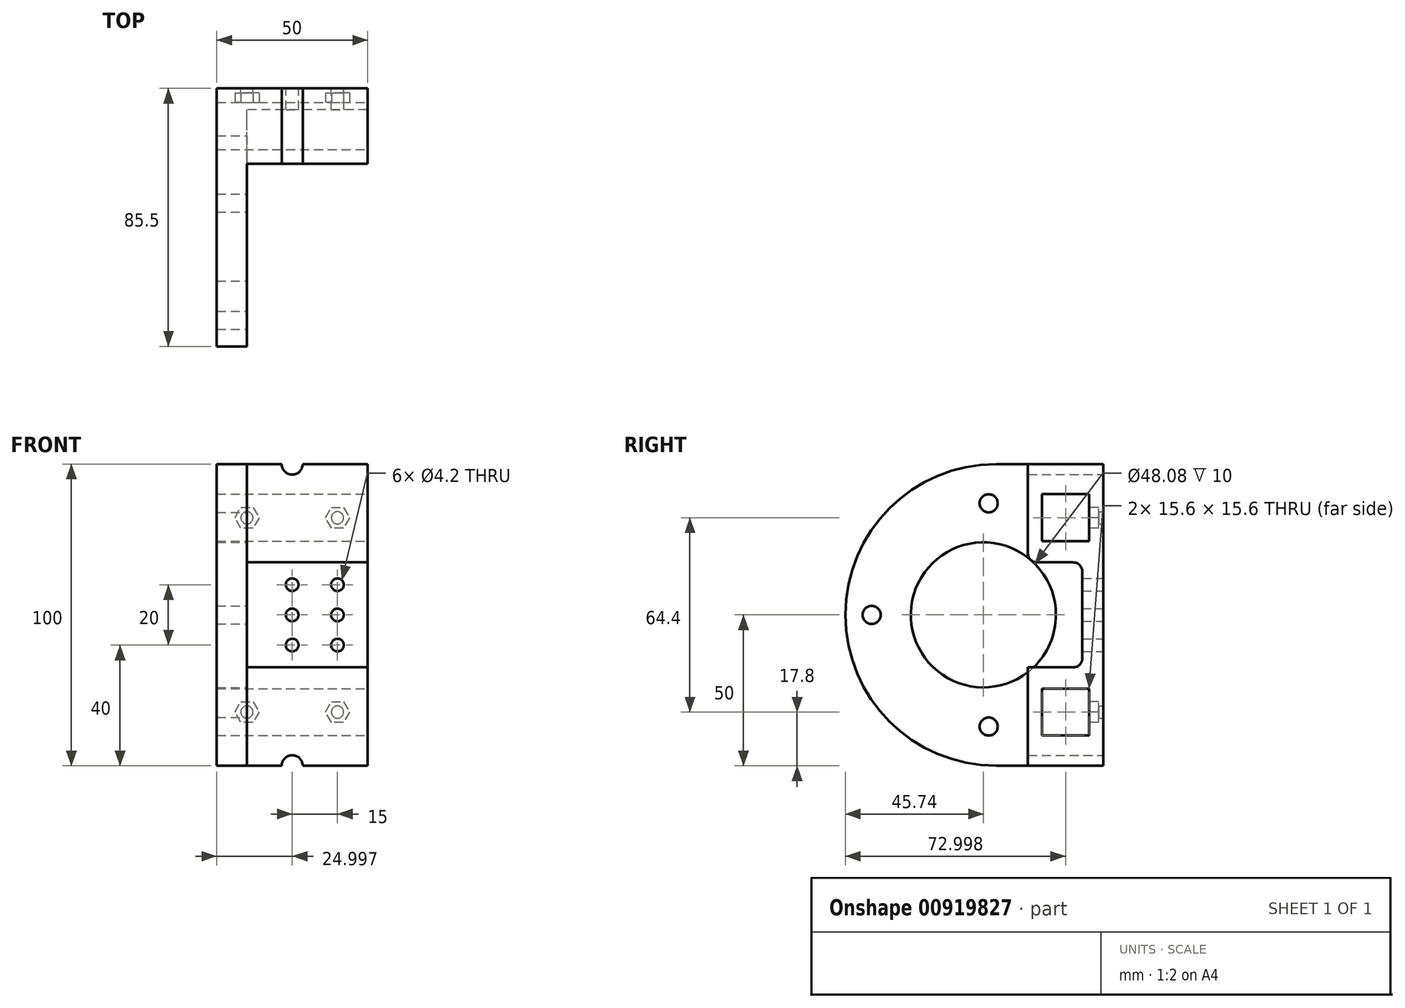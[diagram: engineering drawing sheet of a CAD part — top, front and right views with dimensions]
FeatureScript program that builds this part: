
annotation { "Feature Type Name" : "Feature", "Feature Type Description" : "" }
export const myFeature = defineFeature(function(context is Context, id is Id, definition is map)
    precondition{}
    {
        {
            var Q0;
            Q0=qCreatedBy(makeId("Top.planeOp"),FACE);
            var sketch = newSketch(context, id + "F0", { "sketchPlane" : qUnion([Q0])});
            skLineSegment(sketch, "E0", {"start": v(5.18, 41.2) * mm, "end": v(-44.82, 41.2) * mm});
            skLineSegment(sketch, "E1", {"start": v(-44.82, 41.2) * mm, "end": v(-44.82, -44.3) * mm});
            skLineSegment(sketch, "E2", {"start": v(-44.82, -44.3) * mm, "end": v(-34.82, -44.3) * mm});
            skLineSegment(sketch, "E3", {"start": v(-34.82, -44.3) * mm, "end": v(-34.82, 16.2) * mm});
            skLineSegment(sketch, "E4", {"start": v(-34.82, 16.2) * mm, "end": v(5.18, 16.2) * mm});
            skLineSegment(sketch, "E5", {"start": v(5.18, 16.2) * mm, "end": v(5.18, 41.2) * mm});
            skLineSegment(sketch, "E6.bottom", {"start": v(-27.62, -6.3) * mm, "end": v(-7.62, -6.3) * mm, "construction": true});
            skLineSegment(sketch, "E6.top", {"start": v(-27.62, -26.3) * mm, "end": v(-7.62, -26.3) * mm, "construction": true});
            skLineSegment(sketch, "E6.left", {"start": v(-27.62, -6.3) * mm, "end": v(-27.62, -26.3) * mm, "construction": true});
            skLineSegment(sketch, "E6.right", {"start": v(-7.62, -6.3) * mm, "end": v(-7.62, -26.3) * mm, "construction": true});
            skSolve(sketch);
        }
        {
            var Q0;
            Q0=makeQuery(id+"F0.imprint","IMPRINT",FACE,{"disambiguationData":[TD([[makeQuery(id+"F0.imprint","IMPRINT",EDGE,{"derivedFrom":sQuery(id+"F0.wireOp",EDGE,"E0")}),1.0]])]});
            var Q1;
            Q1 = qSketchRegion(id + "F0", true);
            extrude(context, id + "F1", {"entities" : qUnion([Q0, Q1]), "depth" : 100 * mm, "offsetDistance" : 25 * mm});
        }
        {
            var Q0;
            Q0=makeQuery(id+"F1.opExtrude","SWEPT_FACE",FACE,{"disambiguationData":[OSD([sQuery(id+"F0.wireOp",EDGE,"E5")])]});
            var sketch = newSketch(context, id + "F2", { "sketchPlane" : qUnion([Q0])});
            skLineSegment(sketch, "E7.bottom", {"start": v(36.5, 10) * mm, "end": v(20.9, 10) * mm});
            skLineSegment(sketch, "E7.top", {"start": v(36.5, 25.6) * mm, "end": v(20.9, 25.6) * mm});
            skLineSegment(sketch, "E7.left", {"start": v(36.5, 10) * mm, "end": v(36.5, 25.6) * mm});
            skLineSegment(sketch, "E7.right", {"start": v(20.9, 10) * mm, "end": v(20.9, 25.6) * mm});
            skPoint(sketch, "E7.middle", {"position": v(28.7, 17.8) * mm});
            skPoint(sketch, "E7.middle.positionSnap0", {"position": v(28.7, 0) * mm});
            skPoint(sketch, "E7.centerSnap0", {"position": v(28.7, 0) * mm});
            skLineSegment(sketch, "E8.bottom", {"start": v(36.5, 74.4) * mm, "end": v(20.9, 74.4) * mm});
            skLineSegment(sketch, "E8.top", {"start": v(36.5, 90) * mm, "end": v(20.9, 90) * mm});
            skLineSegment(sketch, "E8.left", {"start": v(36.5, 74.4) * mm, "end": v(36.5, 90) * mm});
            skLineSegment(sketch, "E8.right", {"start": v(20.9, 74.4) * mm, "end": v(20.9, 90) * mm});
            skPoint(sketch, "E8.middle", {"position": v(28.7, 82.2) * mm});
            skPoint(sketch, "E8.middle.positionSnap0", {"position": v(28.7, 100) * mm});
            skPoint(sketch, "E8.centerSnap0", {"position": v(28.7, 100) * mm});
            skSolve(sketch);
        }
        {
            var Q0;
            Q0 = qSketchRegion(id + "F2", true);
            extrude(context, id + "F3", {"entities" : qUnion([Q0]), "operationType" : NewBodyOperationType.REMOVE, "oppositeDirection" : true, "depth" : 134.9 * mm, "offsetDistance" : 25 * mm});
        }
        {
            var Q0;
            Q0=makeQuery(id+"F3.boolean.opBoolean","COPY",FACE,{"derivedFrom":makeQuery(id+"F3.opExtrude","SWEPT_FACE",FACE,{"disambiguationData":[OSD([sQuery(id+"F2.wireOp",EDGE,"E8.left")])]})});
            var sketch = newSketch(context, id + "F4", { "sketchPlane" : qUnion([Q0])});
            skCircle(sketch, "E9.cCircle", {"center": v(-4.82, 82.2) * mm, "radius": 3.46 * mm, "construction": true});
            skLineSegment(sketch, "E9.0", {"start": v(-6.82, 85.66) * mm, "end": v(-2.82, 85.66) * mm});
            skLineSegment(sketch, "E9.1", {"start": v(-2.82, 85.66) * mm, "end": v(-0.83, 82.2) * mm});
            skLineSegment(sketch, "E9.2", {"start": v(-0.83, 82.2) * mm, "end": v(-2.82, 78.74) * mm});
            skLineSegment(sketch, "E9.3", {"start": v(-2.82, 78.74) * mm, "end": v(-6.82, 78.74) * mm});
            skLineSegment(sketch, "E9.4", {"start": v(-6.82, 78.74) * mm, "end": v(-8.82, 82.2) * mm});
            skLineSegment(sketch, "E9.5", {"start": v(-8.82, 82.2) * mm, "end": v(-6.82, 85.66) * mm});
            skPoint(sketch, "E9.0.midPoint", {"position": v(-4.82, 85.66) * mm});
            skCircle(sketch, "E10.cCircle", {"center": v(-34.82, 82.2) * mm, "radius": 3.46 * mm, "construction": true});
            skLineSegment(sketch, "E10.0", {"start": v(-36.82, 85.66) * mm, "end": v(-32.82, 85.66) * mm});
            skLineSegment(sketch, "E10.1", {"start": v(-32.82, 85.66) * mm, "end": v(-30.83, 82.2) * mm});
            skLineSegment(sketch, "E10.2", {"start": v(-30.83, 82.2) * mm, "end": v(-32.82, 78.74) * mm});
            skLineSegment(sketch, "E10.3", {"start": v(-32.82, 78.74) * mm, "end": v(-36.82, 78.74) * mm});
            skLineSegment(sketch, "E10.4", {"start": v(-36.82, 78.74) * mm, "end": v(-38.82, 82.2) * mm});
            skLineSegment(sketch, "E10.5", {"start": v(-38.82, 82.2) * mm, "end": v(-36.82, 85.66) * mm});
            skPoint(sketch, "E10.0.midPoint", {"position": v(-34.82, 85.66) * mm});
            skCircle(sketch, "E11.cCircle", {"center": v(-34.82, 17.8) * mm, "radius": 3.46 * mm, "construction": true});
            skLineSegment(sketch, "E11.0", {"start": v(-36.82, 21.26) * mm, "end": v(-32.82, 21.26) * mm});
            skLineSegment(sketch, "E11.1", {"start": v(-32.82, 21.26) * mm, "end": v(-30.83, 17.8) * mm});
            skLineSegment(sketch, "E11.2", {"start": v(-30.83, 17.8) * mm, "end": v(-32.82, 14.34) * mm});
            skLineSegment(sketch, "E11.3", {"start": v(-32.82, 14.34) * mm, "end": v(-36.82, 14.34) * mm});
            skLineSegment(sketch, "E11.4", {"start": v(-36.82, 14.34) * mm, "end": v(-38.82, 17.8) * mm});
            skLineSegment(sketch, "E11.5", {"start": v(-38.82, 17.8) * mm, "end": v(-36.82, 21.26) * mm});
            skPoint(sketch, "E11.0.midPoint", {"position": v(-34.82, 21.26) * mm});
            skPoint(sketch, "E12", {"position": v(-44.82, 82.2) * mm});
            skCircle(sketch, "E13.cCircle", {"center": v(-4.82, 17.8) * mm, "radius": 3.46 * mm, "construction": true});
            skLineSegment(sketch, "E13.0", {"start": v(-6.82, 21.26) * mm, "end": v(-2.82, 21.26) * mm});
            skLineSegment(sketch, "E13.1", {"start": v(-2.82, 21.26) * mm, "end": v(-0.83, 17.8) * mm});
            skLineSegment(sketch, "E13.2", {"start": v(-0.83, 17.8) * mm, "end": v(-2.82, 14.34) * mm});
            skLineSegment(sketch, "E13.3", {"start": v(-2.82, 14.34) * mm, "end": v(-6.82, 14.34) * mm});
            skLineSegment(sketch, "E13.4", {"start": v(-6.82, 14.34) * mm, "end": v(-8.82, 17.8) * mm});
            skLineSegment(sketch, "E13.5", {"start": v(-8.82, 17.8) * mm, "end": v(-6.82, 21.26) * mm});
            skPoint(sketch, "E13.0.midPoint", {"position": v(-4.82, 21.26) * mm});
            skSolve(sketch);
        }
        {
            var Q0;
            Q0 = qSketchRegion(id + "F4", true);
            extrude(context, id + "F5", {"entities" : qUnion([Q0]), "operationType" : NewBodyOperationType.REMOVE, "oppositeDirection" : true, "depth" : 3.2 * mm, "offsetDistance" : 25 * mm});
        }
        {
            var Q0;
            Q0=makeQuery(id+"F1.opExtrude","SWEPT_FACE",FACE,{"disambiguationData":[OSD([sQuery(id+"F0.wireOp",EDGE,"E0")])]});
            var sketch = newSketch(context, id + "F6", { "sketchPlane" : qUnion([Q0])});
            skCircle(sketch, "E14", {"center": v(34.82, 82.2) * mm, "radius": 2.02 * mm});
            skCircle(sketch, "E15", {"center": v(4.82, 17.8) * mm, "radius": 2.02 * mm});
            skCircle(sketch, "E16", {"center": v(34.82, 17.8) * mm, "radius": 2.02 * mm});
            skCircle(sketch, "E17", {"center": v(4.82, 82.2) * mm, "radius": 2.02 * mm});
            skSolve(sketch);
        }
        {
            var Q0;
            Q0 = qSketchRegion(id + "F6", true);
            extrude(context, id + "F7", {"entities" : qUnion([Q0]), "operationType" : NewBodyOperationType.REMOVE, "oppositeDirection" : true, "depth" : 10 * mm, "offsetDistance" : 25 * mm});
        }
        {
            var Q0;
            Q0=makeQuery(id+"F1.opExtrude","SWEPT_FACE",FACE,{"disambiguationData":[OSD([sQuery(id+"F0.wireOp",EDGE,"E3")])]});
            var sketch = newSketch(context, id + "F8", { "sketchPlane" : qUnion([Q0])});
            skCircle(sketch, "E18", {"center": v(3.2, 87) * mm, "radius": 3 * mm});
            skCircle(sketch, "E19", {"center": v(3.2, 13) * mm, "radius": 3 * mm});
            skCircle(sketch, "E20", {"center": v(-35.6, 50) * mm, "radius": 3 * mm});
            skCircle(sketch, "E21", {"center": v(1.44, 50) * mm, "radius": 24.04 * mm});
            skSolve(sketch);
        }
        {
            var Q0;
            Q0 = qSketchRegion(id + "F8", true);
            extrude(context, id + "F9", {"entities" : qUnion([Q0]), "operationType" : NewBodyOperationType.REMOVE, "oppositeDirection" : true, "depth" : 15 * mm, "offsetDistance" : 25 * mm});
        }
        {
            var Q0;
            Q0=makeQuery(id+"F1.opExtrude","CAP_EDGE",EDGE,{"disambiguationData":[OSD([sQuery(id+"F0.wireOp",EDGE,"E2")])],"isStart":false});
            var Q1;
            Q1=makeQuery(id+"F1.opExtrude","CAP_EDGE",EDGE,{"disambiguationData":[OSD([sQuery(id+"F0.wireOp",EDGE,"E2")])],"isStart":true});
            fillet(context, id + "F10", {"entities" : qUnion([Q0, Q1]), "radius" : 50 * mm, "tangentPropagation" : true, "allowEdgeOverflow" : false});
        }
        {
            var Q0;
            Q0=makeQuery(id+"F1.opExtrude","SWEPT_FACE",FACE,{"disambiguationData":[OSD([sQuery(id+"F0.wireOp",EDGE,"E3")])]});
            var sketch = newSketch(context, id + "F11", { "sketchPlane" : qUnion([Q0])});
            skLineSegment(sketch, "E22.bottom", {"start": v(16.2, 67.4) * mm, "end": v(34.2, 67.4) * mm});
            skLineSegment(sketch, "E22.top", {"start": v(16.2, 32.6) * mm, "end": v(34.2, 32.6) * mm});
            skLineSegment(sketch, "E22.left", {"start": v(16.2, 67.4) * mm, "end": v(16.2, 32.6) * mm});
            skLineSegment(sketch, "E22.right", {"start": v(34.2, 67.4) * mm, "end": v(34.2, 32.6) * mm});
            skSolve(sketch);
        }
        {
            var Q0;
            Q0 = qSketchRegion(id + "F11", true);
            extrude(context, id + "F12", {"entities" : qUnion([Q0]), "operationType" : NewBodyOperationType.REMOVE, "depth" : 100 * mm, "offsetDistance" : 25 * mm});
        }
        {
            var Q0;
            Q0=makeQuery(id+"F1.opExtrude","SWEPT_FACE",FACE,{"disambiguationData":[OSD([sQuery(id+"F0.wireOp",EDGE,"E0")])]});
            var sketch = newSketch(context, id + "F13", { "sketchPlane" : qUnion([Q0])});
            skCircle(sketch, "E23", {"center": v(19.82, 0) * mm, "radius": 3.5 * mm});
            skCircle(sketch, "E24", {"center": v(19.82, 100) * mm, "radius": 3.5 * mm});
            skSolve(sketch);
        }
        {
            var Q0;
            Q0 = qSketchRegion(id + "F13", true);
            extrude(context, id + "F14", {"entities" : qUnion([Q0]), "operationType" : NewBodyOperationType.REMOVE, "oppositeDirection" : true, "depth" : 50 * mm, "offsetDistance" : 25 * mm});
        }
        {
            var Q0;
            Q0=makeQuery(id+"F1.opExtrude","SWEPT_FACE",FACE,{"disambiguationData":[OSD([sQuery(id+"F0.wireOp",EDGE,"E0")])]});
            var sketch = newSketch(context, id + "F15", { "sketchPlane" : qUnion([Q0])});
            skCircle(sketch, "E25", {"center": v(19.82, 50) * mm, "radius": 2.1 * mm});
            skPoint(sketch, "E25.centerSnap0", {"position": v(19.82, 3.5) * mm});
            skPoint(sketch, "E25.centerSnap1", {"position": v(-5.18, 50) * mm});
            skCircle(sketch, "E26", {"center": v(19.82, 60) * mm, "radius": 2.1 * mm});
            skCircle(sketch, "E27", {"center": v(19.82, 40) * mm, "radius": 2.1 * mm});
            skCircle(sketch, "E28", {"center": v(4.82, 50) * mm, "radius": 2.1 * mm});
            skCircle(sketch, "E29", {"center": v(4.82, 60) * mm, "radius": 2.1 * mm});
            skCircle(sketch, "E30", {"center": v(4.82, 40) * mm, "radius": 2.1 * mm});
            skSolve(sketch);
        }
        {
            var Q0;
            Q0 = qSketchRegion(id + "F15", true);
            extrude(context, id + "F16", {"entities" : qUnion([Q0]), "operationType" : NewBodyOperationType.REMOVE, "oppositeDirection" : true, "depth" : 25 * mm, "offsetDistance" : 25 * mm});
        }
        {
            var Q0;
            Q0=makeQuery(id+"F12.boolean.opBoolean","COPY",EDGE,{"derivedFrom":makeQuery(id+"F12.opExtrude","SWEPT_EDGE",EDGE,{"disambiguationData":[OSD([sQuery(id+"F0.wireOp",EDGE,"E3"),sQuery(id+"F0.wireOp",EDGE,"E4"),sQuery(id+"F11.wireOp",EDGE,"E22.bottom"),sQuery(id+"F11.wireOp",EDGE,"E22.left")])]})});
            var Q1;
            Q1=makeQuery(id+"F12.boolean.opBoolean","COPY",EDGE,{"derivedFrom":makeQuery(id+"F12.opExtrude","SWEPT_EDGE",EDGE,{"disambiguationData":[OSD([sQuery(id+"F11.wireOp",EDGE,"E22.bottom"),sQuery(id+"F11.wireOp",EDGE,"E22.right")])]})});
            var Q2;
            Q2=makeQuery(id+"F12.boolean.opBoolean","COPY",EDGE,{"derivedFrom":makeQuery(id+"F12.opExtrude","SWEPT_EDGE",EDGE,{"disambiguationData":[OSD([sQuery(id+"F11.wireOp",EDGE,"E22.top"),sQuery(id+"F11.wireOp",EDGE,"E22.right")])]})});
            var Q3;
            Q3=makeQuery(id+"F12.boolean.opBoolean","COPY",EDGE,{"derivedFrom":makeQuery(id+"F12.opExtrude","SWEPT_EDGE",EDGE,{"disambiguationData":[OSD([sQuery(id+"F0.wireOp",EDGE,"E3"),sQuery(id+"F0.wireOp",EDGE,"E4"),sQuery(id+"F11.wireOp",EDGE,"E22.top"),sQuery(id+"F11.wireOp",EDGE,"E22.left")])]})});
            fillet(context, id + "F17", {"entities" : qUnion([Q0, Q1, Q2, Q3]), "radius" : 3 * mm, "tangentPropagation" : true, "allowEdgeOverflow" : false});
        }
    });
